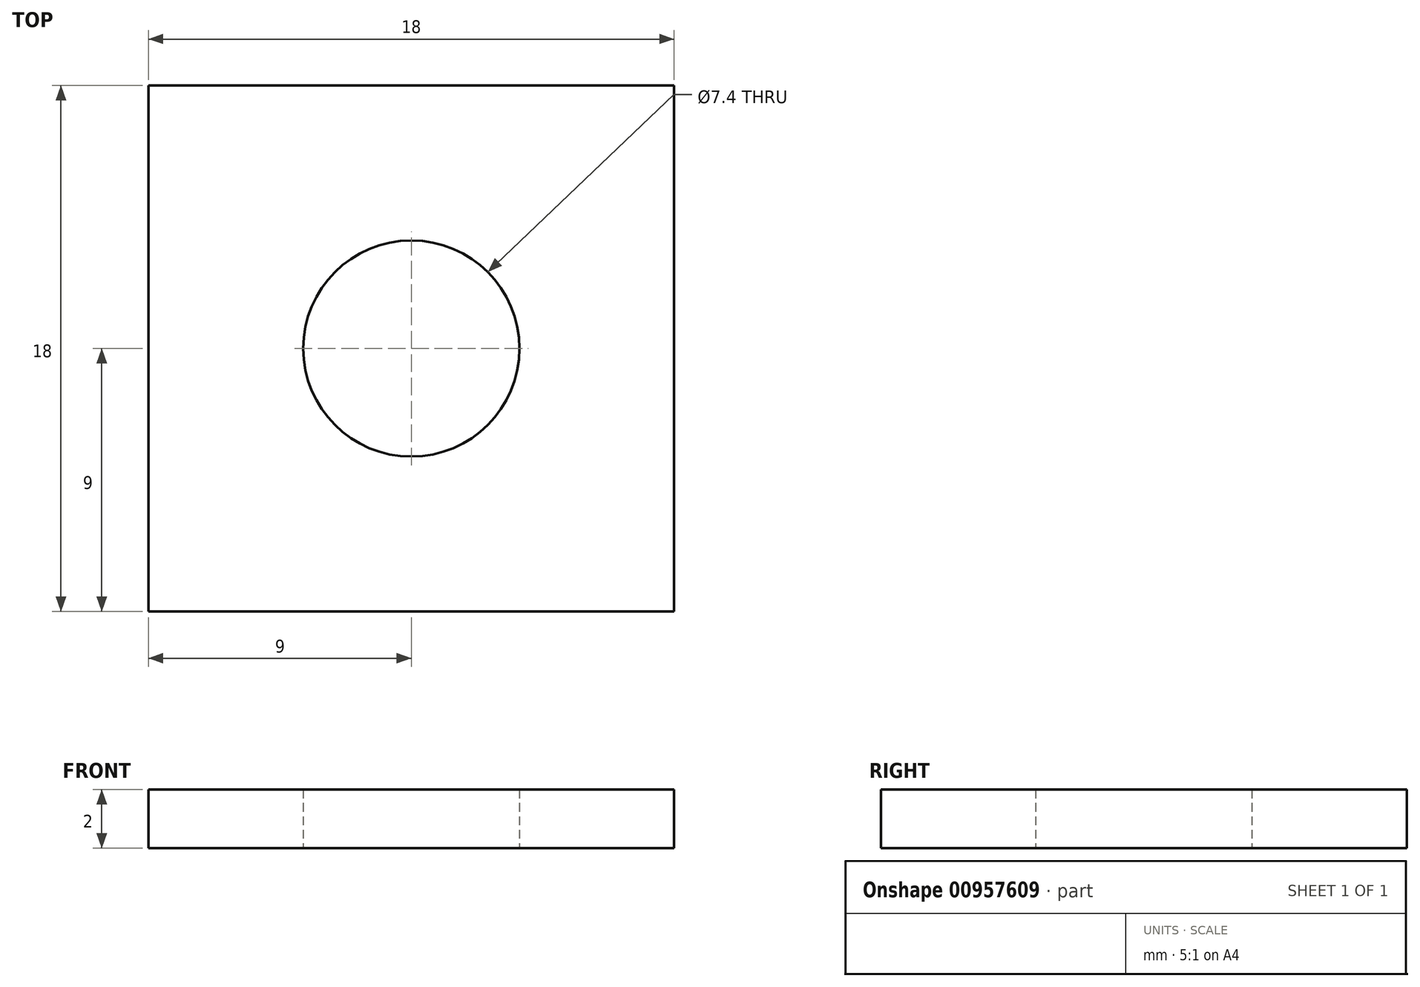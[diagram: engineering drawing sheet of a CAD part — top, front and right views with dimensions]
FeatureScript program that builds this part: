
annotation { "Feature Type Name" : "Feature", "Feature Type Description" : "" }
export const myFeature = defineFeature(function(context is Context, id is Id, definition is map)
    precondition{}
    {
        {
            var Q0;
            Q0=qCreatedBy(makeId("Top.planeOp"),FACE);
            var sketch = newSketch(context, id + "F0", { "sketchPlane" : qUnion([Q0])});
            skLineSegment(sketch, "E0.bottom", {"start": v(-9, 9) * mm, "end": v(9, 9) * mm});
            skLineSegment(sketch, "E0.top", {"start": v(-9, -9) * mm, "end": v(9, -9) * mm});
            skLineSegment(sketch, "E0.left", {"start": v(-9, 9) * mm, "end": v(-9, -9) * mm});
            skLineSegment(sketch, "E0.right", {"start": v(9, 9) * mm, "end": v(9, -9) * mm});
            skPoint(sketch, "E0.middle", {"position": v(0, 0) * mm});
            skCircle(sketch, "E1", {"center": v(0, 0) * mm, "radius": 3.7 * mm});
            skSolve(sketch);
        }
        {
            var Q0;
            Q0=qCreatedBy(makeId("Top.planeOp"),FACE);
            cPlane(context, id + "F1", {"entities" : qUnion([Q0]), "cplaneType" : CPlaneType.OFFSET, "offset" : 2 * mm, "width" : 150 * mm, "height" : 150 * mm});
        }
        {
            var Q0;
            Q0=makeQuery(id+"F0.imprint","IMPRINT",FACE,{"disambiguationData":[TD([[makeQuery(id+"F0.imprint","IMPRINT",EDGE,{"derivedFrom":sQuery(id+"F0.wireOp",EDGE,"E0.bottom")}),-1.0]])]});
            extrude(context, id + "F2", {"entities" : qUnion([Q0]), "depth" : 2 * mm, "offsetDistance" : 25 * mm});
        }
    });
